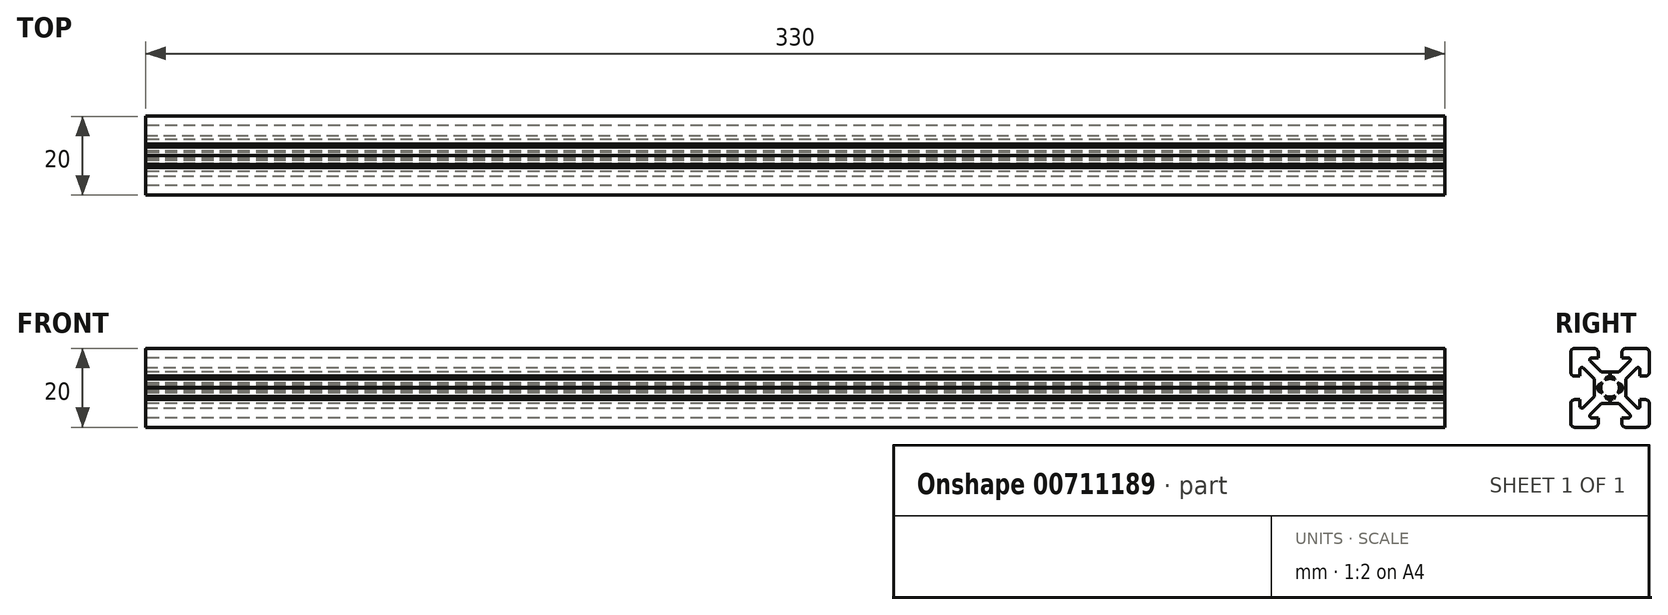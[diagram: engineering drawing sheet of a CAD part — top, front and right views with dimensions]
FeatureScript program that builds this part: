
annotation { "Feature Type Name" : "Feature", "Feature Type Description" : "" }
export const myFeature = defineFeature(function(context is Context, id is Id, definition is map)
    precondition{}
    {
        {
            var Q0;
            Q0=qCreatedBy(makeId("Top.planeOp"),FACE);
            var sketch = newSketch(context, id + "F0", { "sketchPlane" : qUnion([Q0])});
            skLineSegment(sketch, "E0", {"start": v(-15.81, 0) * mm, "end": v(2.4, 0) * mm, "construction": true});
            skLineSegment(sketch, "E1", {"start": v(0, 15.89) * mm, "end": v(0, -13.7) * mm, "construction": true});
            skLineSegment(sketch, "E2", {"start": v(0, 0) * mm, "end": v(-1.66, 1.66) * mm, "construction": true});
            skLineSegment(sketch, "E3", {"start": v(-2.3, 4.06) * mm, "end": v(-5.86, 7.63) * mm});
            skLineSegment(sketch, "E4", {"start": v(-5.86, 7.63) * mm, "end": v(-3, 7.63) * mm});
            skLineSegment(sketch, "E5", {"start": v(-3, 7.63) * mm, "end": v(-3, 10) * mm});
            skLineSegment(sketch, "E6", {"start": v(-3, 10) * mm, "end": v(-10, 10) * mm});
            skLineSegment(sketch, "E7.MirrorCS", {"start": v(-4, 2.23) * mm, "end": v(-7.63, 5.86) * mm});
            skLineSegment(sketch, "E8.MirrorCS", {"start": v(-7.63, 3) * mm, "end": v(-10, 3) * mm});
            skLineSegment(sketch, "E9.MirrorCS", {"start": v(-10, 3) * mm, "end": v(-10, 10) * mm});
            skLineSegment(sketch, "E10.MirrorCS", {"start": v(-7.63, 5.86) * mm, "end": v(-7.63, 3) * mm});
            skLineSegment(sketch, "E11.MirrorCS", {"start": v(3, 10) * mm, "end": v(10, 10) * mm});
            skLineSegment(sketch, "E12.MirrorCS", {"start": v(5.86, 7.63) * mm, "end": v(3, 7.63) * mm});
            skLineSegment(sketch, "E13.MirrorCS", {"start": v(3, 7.63) * mm, "end": v(3, 10) * mm});
            skLineSegment(sketch, "E14.MirrorCS", {"start": v(7.63, 5.86) * mm, "end": v(7.63, 3) * mm});
            skLineSegment(sketch, "E15.MirrorCS", {"start": v(10, 3) * mm, "end": v(10, 10) * mm});
            skLineSegment(sketch, "E16.MirrorCS", {"start": v(7.63, 3) * mm, "end": v(10, 3) * mm});
            skLineSegment(sketch, "E17.MirrorCS", {"start": v(2.3, 4.06) * mm, "end": v(5.86, 7.63) * mm});
            skLineSegment(sketch, "E18.MirrorCS", {"start": v(4, 2.23) * mm, "end": v(7.63, 5.86) * mm});
            skLineSegment(sketch, "E19.MirrorCS", {"start": v(5.86, -7.63) * mm, "end": v(3, -7.63) * mm});
            skLineSegment(sketch, "E20.MirrorCS", {"start": v(3, -10) * mm, "end": v(10, -10) * mm});
            skLineSegment(sketch, "E21.MirrorCS", {"start": v(-5.86, -7.63) * mm, "end": v(-3, -7.63) * mm});
            skLineSegment(sketch, "E22.MirrorCS", {"start": v(-3, -10) * mm, "end": v(-10, -10) * mm});
            skLineSegment(sketch, "E23.MirrorCS", {"start": v(-3, -7.63) * mm, "end": v(-3, -10) * mm});
            skLineSegment(sketch, "E24.MirrorCS", {"start": v(3, -7.63) * mm, "end": v(3, -10) * mm});
            skLineSegment(sketch, "E25.MirrorCS", {"start": v(7.63, -5.86) * mm, "end": v(7.63, -3) * mm});
            skLineSegment(sketch, "E26.MirrorCS", {"start": v(10, -3) * mm, "end": v(10, -10) * mm});
            skLineSegment(sketch, "E27.MirrorCS", {"start": v(4, -2.23) * mm, "end": v(7.63, -5.86) * mm});
            skLineSegment(sketch, "E28.MirrorCS", {"start": v(-7.63, -5.86) * mm, "end": v(-7.63, -3) * mm});
            skLineSegment(sketch, "E29.MirrorCS", {"start": v(-10, -3) * mm, "end": v(-10, -10) * mm});
            skLineSegment(sketch, "E30.MirrorCS", {"start": v(-7.63, -3) * mm, "end": v(-10, -3) * mm});
            skLineSegment(sketch, "E31.MirrorCS", {"start": v(-4, -2.23) * mm, "end": v(-7.63, -5.86) * mm});
            skLineSegment(sketch, "E32.MirrorCS", {"start": v(2.23, -4) * mm, "end": v(5.86, -7.63) * mm});
            skLineSegment(sketch, "E33.MirrorCS", {"start": v(-2.23, -4) * mm, "end": v(-5.86, -7.63) * mm});
            skLineSegment(sketch, "E34.MirrorCS", {"start": v(7.63, -3) * mm, "end": v(10, -3) * mm});
            skLineSegment(sketch, "E35", {"start": v(-4, 0) * mm, "end": v(-4, 0) * mm});
            skLineSegment(sketch, "E36", {"start": v(-2.3, 4.06) * mm, "end": v(-0.02, 4.06) * mm});
            skLineSegment(sketch, "E37.MirrorCS", {"start": v(-15.81, 8.12) * mm, "end": v(21.32, 8.12) * mm, "construction": true});
            skLineSegment(sketch, "E38", {"start": v(-4, 2.23) * mm, "end": v(-4, 0.02) * mm});
            skLineSegment(sketch, "E39", {"start": v(-2.23, -4) * mm, "end": v(-0.05, -4) * mm});
            skLineSegment(sketch, "E40", {"start": v(4, 2.23) * mm, "end": v(4, 0.03) * mm});
            skPoint(sketch, "E41.orphan", {"position": v(-0.59, 2.36) * mm});
            skPoint(sketch, "E42.orphan", {"position": v(-2.36, 0.59) * mm});
            skLineSegment(sketch, "E43.trimOffspring", {"start": v(0.03, 4.06) * mm, "end": v(2.3, 4.06) * mm});
            skPoint(sketch, "E44.orphan", {"position": v(0.59, 2.36) * mm});
            skPoint(sketch, "E45.orphan", {"position": v(2.36, 0.59) * mm});
            skPoint(sketch, "E46.orphan", {"position": v(-2.36, -0.59) * mm});
            skPoint(sketch, "E47.orphan", {"position": v(-0.59, -2.36) * mm});
            skPoint(sketch, "E48.orphan", {"position": v(0.59, -2.36) * mm});
            skPoint(sketch, "E49.orphan", {"position": v(2.36, -0.59) * mm});
            skLineSegment(sketch, "E50", {"start": v(-2.4, 0.03) * mm, "end": v(-2.4, 0.03) * mm});
            skLineSegment(sketch, "E51.MirrorCS", {"start": v(-2.4, -0.03) * mm, "end": v(-2.4, -0.03) * mm});
            skLineSegment(sketch, "E52.MirrorCS", {"start": v(2.4, 0.03) * mm, "end": v(2.4, 0.03) * mm});
            skLineSegment(sketch, "E53.MirrorCS", {"start": v(2.4, -0.03) * mm, "end": v(2.4, -0.03) * mm});
            skLineSegment(sketch, "E54.trimOffspring", {"start": v(4, -0.03) * mm, "end": v(4, -2.23) * mm});
            skLineSegment(sketch, "E55.trimOffspring", {"start": v(-4, -0.03) * mm, "end": v(-4, -2.23) * mm});
            skPoint(sketch, "E56.end.orphan", {"position": v(-2.4, 0) * mm});
            skPoint(sketch, "E57.orphan", {"position": v(-4, 0.03) * mm});
            skPoint(sketch, "E58.MirrorCS.end.orphan", {"position": v(2.4, 0) * mm});
            skPoint(sketch, "E58.MirrorCS.start.orphan", {"position": v(2.4, -0.03) * mm});
            skPoint(sketch, "E59.MirrorCS.start.orphan", {"position": v(2.4, 0.03) * mm});
            skLineSegment(sketch, "E60.trimOffspring", {"start": v(0.05, -4) * mm, "end": v(2.23, -4) * mm});
            skLineSegment(sketch, "E61", {"start": v(0, 0) * mm, "end": v(10, 10) * mm, "construction": true});
            skLineSegment(sketch, "E62", {"start": v(0, 0) * mm, "end": v(-10, -10) * mm, "construction": true});
            skLineSegment(sketch, "E63", {"start": v(10, -10) * mm, "end": v(0.07, 0.07) * mm, "construction": true});
            skPoint(sketch, "E64.start.orphan", {"position": v(-4, -0.03) * mm});
            skLineSegment(sketch, "E65", {"start": v(-2.82, -0.78) * mm, "end": v(-1.9, -1.37) * mm});
            skPoint(sketch, "E66.orphan", {"position": v(-1.66, -1.66) * mm});
            skPoint(sketch, "E67.orphan", {"position": v(0.03, -4.06) * mm});
            skPoint(sketch, "E68.orphan", {"position": v(-0.03, -4.06) * mm});
            skLineSegment(sketch, "E69", {"start": v(-2.82, 0.8) * mm, "end": v(-1.87, 1.41) * mm});
            skLineSegment(sketch, "E70", {"start": v(-0.76, 2.95) * mm, "end": v(-1.54, 1.77) * mm});
            skLineSegment(sketch, "E71", {"start": v(0.76, 2.95) * mm, "end": v(1.51, 1.8) * mm});
            skLineSegment(sketch, "E72", {"start": v(2.82, 0.8) * mm, "end": v(1.83, 1.46) * mm});
            skLineSegment(sketch, "E73", {"start": v(2.82, -0.8) * mm, "end": v(1.87, -1.41) * mm});
            skLineSegment(sketch, "E74.trimOffspring", {"start": v(1.8, -1.68) * mm, "end": v(1.82, -1.66) * mm});
            skLineSegment(sketch, "E75.trimOffspring", {"start": v(-8.12, 8.12) * mm, "end": v(-29.35, 29.35) * mm, "construction": true});
            skLineSegment(sketch, "E76", {"start": v(0.74, -2.96) * mm, "end": v(1.51, -1.8) * mm});
            skPoint(sketch, "E77.trimOffspring.start.orphan", {"position": v(0.33, -2.4) * mm});
            skPoint(sketch, "E78.MirrorCS.end.orphan", {"position": v(-0.33, -2.4) * mm});
            skLineSegment(sketch, "E79.trimOffspring", {"start": v(2.43, 0) * mm, "end": v(21.32, 0) * mm, "construction": true});
            skPoint(sketch, "E80.trimOffspring.start.orphan", {"position": v(0.33, 2.4) * mm});
            skPoint(sketch, "E81.trimOffspring.start.orphan", {"position": v(-0.33, 2.4) * mm});
            skArc(sketch, "E82", {"start": v(-1.87, 1.41) * mm, "mid": v(-2.35, 0.03) * mm, "end": v(-1.9, -1.37) * mm});
            skArc(sketch, "E83.trimOffspring", {"start": v(1.51, 1.8) * mm, "mid": v(-0.02, 2.35) * mm, "end": v(-1.54, 1.77) * mm});
            skArc(sketch, "E84.trimOffspring", {"start": v(1.87, -1.41) * mm, "mid": v(2.35, 0.03) * mm, "end": v(1.83, 1.46) * mm});
            skArc(sketch, "E85.trimOffspring", {"start": v(-1.55, -1.76) * mm, "mid": v(-0.03, -2.35) * mm, "end": v(1.51, -1.8) * mm});
            skLineSegment(sketch, "E86", {"start": v(-1.55, -1.76) * mm, "end": v(-0.75, -2.96) * mm});
            skLineSegment(sketch, "E87", {"start": v(-4, 0.03) * mm, "end": v(-2.82, 0.03) * mm});
            skLineSegment(sketch, "E88", {"start": v(-2.82, 0.03) * mm, "end": v(-2.82, 0.8) * mm});
            skLineSegment(sketch, "E89", {"start": v(-4, -0.03) * mm, "end": v(-2.82, -0.03) * mm});
            skLineSegment(sketch, "E90", {"start": v(-2.82, -0.03) * mm, "end": v(-2.82, -0.78) * mm});
            skLineSegment(sketch, "E91.MirrorCS", {"start": v(4, 0.03) * mm, "end": v(2.82, 0.03) * mm});
            skLineSegment(sketch, "E92.MirrorCS", {"start": v(4, -0.03) * mm, "end": v(2.82, -0.03) * mm});
            skLineSegment(sketch, "E93", {"start": v(2.82, 0.03) * mm, "end": v(2.82, 0.8) * mm});
            skLineSegment(sketch, "E94", {"start": v(2.82, -0.03) * mm, "end": v(2.82, -0.8) * mm});
            skLineSegment(sketch, "E95", {"start": v(-0.05, -4) * mm, "end": v(-0.05, -2.96) * mm});
            skLineSegment(sketch, "E96", {"start": v(-0.05, -2.96) * mm, "end": v(-0.75, -2.96) * mm});
            skLineSegment(sketch, "E97", {"start": v(0.05, -4) * mm, "end": v(0.05, -2.96) * mm});
            skLineSegment(sketch, "E98", {"start": v(0.05, -2.96) * mm, "end": v(0.74, -2.96) * mm});
            skLineSegment(sketch, "E99", {"start": v(-0.02, 4.06) * mm, "end": v(-0.02, 2.95) * mm});
            skLineSegment(sketch, "E100", {"start": v(-0.02, 2.95) * mm, "end": v(-0.76, 2.95) * mm});
            skLineSegment(sketch, "E101", {"start": v(0.03, 4.06) * mm, "end": v(0.03, 2.95) * mm});
            skLineSegment(sketch, "E102", {"start": v(0.03, 2.95) * mm, "end": v(0.76, 2.95) * mm});
            skSolve(sketch);
        }
        {
            var Q0;
            Q0=qSketchRegion(id+"F0",true);
            extrude(context, id + "F1", {"entities" : qUnion([Q0]), "depth" : 330 * mm});
        }
        {
            var Q0;
            Q0=makeQuery(id+"F1.opExtrude","SWEPT_EDGE",EDGE,{"disambiguationData":[OSD([sQuery(id+"F0.wireOp",EDGE,"E15.MirrorCS"),sQuery(id+"F0.wireOp",EDGE,"E11.MirrorCS")])]});
            var Q1;
            Q1=makeQuery(id+"F1.opExtrude","SWEPT_EDGE",EDGE,{"disambiguationData":[OSD([sQuery(id+"F0.wireOp",EDGE,"E20.MirrorCS"),sQuery(id+"F0.wireOp",EDGE,"E26.MirrorCS")])]});
            var Q2;
            Q2=makeQuery(id+"F1.opExtrude","SWEPT_EDGE",EDGE,{"disambiguationData":[OSD([sQuery(id+"F0.wireOp",EDGE,"E22.MirrorCS"),sQuery(id+"F0.wireOp",EDGE,"E29.MirrorCS")])]});
            var Q3;
            Q3=makeQuery(id+"F1.opExtrude","SWEPT_EDGE",EDGE,{"disambiguationData":[OSD([sQuery(id+"F0.wireOp",EDGE,"E22.MirrorCS"),sQuery(id+"F0.wireOp",EDGE,"E23.MirrorCS")])]});
            var Q4;
            Q4=makeQuery(id+"F1.opExtrude","SWEPT_EDGE",EDGE,{"disambiguationData":[OSD([sQuery(id+"F0.wireOp",EDGE,"E20.MirrorCS"),sQuery(id+"F0.wireOp",EDGE,"E24.MirrorCS")])]});
            var Q5;
            Q5=makeQuery(id+"F1.opExtrude","SWEPT_EDGE",EDGE,{"disambiguationData":[OSD([sQuery(id+"F0.wireOp",EDGE,"E5"),sQuery(id+"F0.wireOp",EDGE,"E6")])]});
            var Q6;
            Q6=makeQuery(id+"F1.opExtrude","SWEPT_EDGE",EDGE,{"disambiguationData":[OSD([sQuery(id+"F0.wireOp",EDGE,"E8.MirrorCS"),sQuery(id+"F0.wireOp",EDGE,"E9.MirrorCS")])]});
            var Q7;
            Q7=makeQuery(id+"F1.opExtrude","SWEPT_EDGE",EDGE,{"disambiguationData":[OSD([sQuery(id+"F0.wireOp",EDGE,"E15.MirrorCS"),sQuery(id+"F0.wireOp",EDGE,"E16.MirrorCS")])]});
            var Q8;
            Q8=makeQuery(id+"F1.opExtrude","SWEPT_EDGE",EDGE,{"disambiguationData":[OSD([sQuery(id+"F0.wireOp",EDGE,"E26.MirrorCS"),sQuery(id+"F0.wireOp",EDGE,"E34.MirrorCS")])]});
            var Q9;
            Q9=makeQuery(id+"F1.opExtrude","SWEPT_EDGE",EDGE,{"disambiguationData":[OSD([sQuery(id+"F0.wireOp",EDGE,"E29.MirrorCS"),sQuery(id+"F0.wireOp",EDGE,"E30.MirrorCS")])]});
            var Q10;
            Q10=makeQuery(id+"F1.opExtrude","SWEPT_EDGE",EDGE,{"disambiguationData":[OSD([sQuery(id+"F0.wireOp",EDGE,"E9.MirrorCS"),sQuery(id+"F0.wireOp",EDGE,"E6")])]});
            var Q11;
            Q11=makeQuery(id+"F1.opExtrude","SWEPT_EDGE",EDGE,{"disambiguationData":[OSD([sQuery(id+"F0.wireOp",EDGE,"E13.MirrorCS"),sQuery(id+"F0.wireOp",EDGE,"E11.MirrorCS")])]});
            fillet(context, id + "F2", {"entities" : qUnion([Q0, Q1, Q2, Q3, Q4, Q5, Q6, Q7, Q8, Q9, Q10, Q11]), "radius" : 1 * mm, "tangentPropagation" : true, "allowEdgeOverflow" : false});
        }
        {
            var Q0;
            Q0=makeQuery(id+"F1.opExtrude","SWEPT_EDGE",EDGE,{"disambiguationData":[OSD([sQuery(id+"F0.wireOp",EDGE,"E7.MirrorCS"),sQuery(id+"F0.wireOp",EDGE,"E10.MirrorCS")])]});
            var Q1;
            Q1=makeQuery(id+"F1.opExtrude","SWEPT_EDGE",EDGE,{"disambiguationData":[OSD([sQuery(id+"F0.wireOp",EDGE,"E3"),sQuery(id+"F0.wireOp",EDGE,"E4")])]});
            var Q2;
            Q2=makeQuery(id+"F1.opExtrude","SWEPT_EDGE",EDGE,{"disambiguationData":[OSD([sQuery(id+"F0.wireOp",EDGE,"E12.MirrorCS"),sQuery(id+"F0.wireOp",EDGE,"E17.MirrorCS")])]});
            var Q3;
            Q3=makeQuery(id+"F1.opExtrude","SWEPT_EDGE",EDGE,{"disambiguationData":[OSD([sQuery(id+"F0.wireOp",EDGE,"E14.MirrorCS"),sQuery(id+"F0.wireOp",EDGE,"E18.MirrorCS")])]});
            var Q4;
            Q4=makeQuery(id+"F1.opExtrude","SWEPT_EDGE",EDGE,{"disambiguationData":[OSD([sQuery(id+"F0.wireOp",EDGE,"E28.MirrorCS"),sQuery(id+"F0.wireOp",EDGE,"E31.MirrorCS")])]});
            var Q5;
            Q5=makeQuery(id+"F1.opExtrude","SWEPT_EDGE",EDGE,{"disambiguationData":[OSD([sQuery(id+"F0.wireOp",EDGE,"E21.MirrorCS"),sQuery(id+"F0.wireOp",EDGE,"E33.MirrorCS")])]});
            var Q6;
            Q6=makeQuery(id+"F1.opExtrude","SWEPT_EDGE",EDGE,{"disambiguationData":[OSD([sQuery(id+"F0.wireOp",EDGE,"E19.MirrorCS"),sQuery(id+"F0.wireOp",EDGE,"E32.MirrorCS")])]});
            var Q7;
            Q7=makeQuery(id+"F1.opExtrude","SWEPT_EDGE",EDGE,{"disambiguationData":[OSD([sQuery(id+"F0.wireOp",EDGE,"E25.MirrorCS"),sQuery(id+"F0.wireOp",EDGE,"E27.MirrorCS")])]});
            fillet(context, id + "F3", {"entities" : qUnion([Q0, Q1, Q2, Q3, Q4, Q5, Q6, Q7]), "radius" : .5 * mm, "tangentPropagation" : true, "allowEdgeOverflow" : false});
        }
        {
            var Q0;
            Q0=makeQuery(id+"F1.opExtrude","SWEPT_EDGE",EDGE,{"disambiguationData":[OSD([sQuery(id+"F0.wireOp",EDGE,"E69"),sQuery(id+"F0.wireOp",EDGE,"E82")])]});
            var Q1;
            Q1=makeQuery(id+"F1.opExtrude","SWEPT_EDGE",EDGE,{"disambiguationData":[OSD([sQuery(id+"F0.wireOp",EDGE,"E17.MirrorCS"),sQuery(id+"F0.wireOp",EDGE,"E43.trimOffspring")])]});
            var Q2;
            {var subQ0=sQuery(id+"F0.wireOp",EDGE,"E12.MirrorCS");Q2=makeQuery(id+"F3.opFillet","BLEND_EDGE",EDGE,{"blendedFrom":[makeQuery(id+"F1.opExtrude","SWEPT_EDGE",EDGE,{"disambiguationData":[OSD([subQ0,sQuery(id+"F0.wireOp",EDGE,"E17.MirrorCS")])]}),makeQuery(id+"F1.opExtrude","SWEPT_FACE",FACE,{"disambiguationData":[OSD([subQ0])]})],"blendedInto":[makeQuery(id+"F1.opExtrude","SWEPT_FACE",FACE,{"disambiguationData":[OSD([subQ0])]})]});}
            var Q3;
            Q3=makeQuery(id+"F1.opExtrude","SWEPT_EDGE",EDGE,{"disambiguationData":[OSD([sQuery(id+"F0.wireOp",EDGE,"E70"),sQuery(id+"F0.wireOp",EDGE,"E83.trimOffspring")])]});
            var Q4;
            Q4=makeQuery(id+"F1.opExtrude","SWEPT_EDGE",EDGE,{"disambiguationData":[OSD([sQuery(id+"F0.wireOp",EDGE,"VnvyymTW-JKNP-Vp1J-SOXt-zXPDHYCny5Fm"),sQuery(id+"F0.wireOp",EDGE,"E85.trimOffspring")])]});
            var Q5;
            Q5=makeQuery(id+"F1.opExtrude","SWEPT_EDGE",EDGE,{"disambiguationData":[OSD([sQuery(id+"F0.wireOp",EDGE,"E76"),sQuery(id+"F0.wireOp",EDGE,"E85.trimOffspring")])]});
            var Q6;
            Q6=makeQuery(id+"F1.opExtrude","SWEPT_EDGE",EDGE,{"disambiguationData":[OSD([sQuery(id+"F0.wireOp",EDGE,"E73"),sQuery(id+"F0.wireOp",EDGE,"E84.trimOffspring")])]});
            var Q7;
            Q7=makeQuery(id+"F1.opExtrude","SWEPT_EDGE",EDGE,{"disambiguationData":[OSD([sQuery(id+"F0.wireOp",EDGE,"E72"),sQuery(id+"F0.wireOp",EDGE,"E84.trimOffspring")])]});
            var Q8;
            Q8=makeQuery(id+"F1.opExtrude","SWEPT_EDGE",EDGE,{"disambiguationData":[OSD([sQuery(id+"F0.wireOp",EDGE,"E71"),sQuery(id+"F0.wireOp",EDGE,"E83.trimOffspring")])]});
            var Q9;
            Q9=makeQuery(id+"F1.opExtrude","SWEPT_EDGE",EDGE,{"disambiguationData":[OSD([sQuery(id+"F0.wireOp",EDGE,"E65"),sQuery(id+"F0.wireOp",EDGE,"E82")])]});
            fillet(context, id + "F4", {"entities" : qUnion([Q0, Q1, Q2, Q3, Q4, Q5, Q6, Q7, Q8, Q9]), "radius" : .1 * mm, "tangentPropagation" : true, "allowEdgeOverflow" : false});
        }
        {
            var Q0;
            Q0=makeQuery(id+"F1.opExtrude","SWEPT_BODY",BODY,{"disambiguationData":[OSD([sQuery(id+"F0.wireOp",EDGE,"E3"),sQuery(id+"F0.wireOp",EDGE,"E7.MirrorCS"),sQuery(id+"F0.wireOp",EDGE,"E8.MirrorCS"),sQuery(id+"F0.wireOp",EDGE,"E9.MirrorCS"),sQuery(id+"F0.wireOp",EDGE,"E10.MirrorCS"),sQuery(id+"F0.wireOp",EDGE,"E5"),sQuery(id+"F0.wireOp",EDGE,"E6"),sQuery(id+"F0.wireOp",EDGE,"E4"),sQuery(id+"F0.wireOp",EDGE,"E14.MirrorCS"),sQuery(id+"F0.wireOp",EDGE,"E15.MirrorCS"),sQuery(id+"F0.wireOp",EDGE,"E16.MirrorCS"),sQuery(id+"F0.wireOp",EDGE,"E12.MirrorCS"),sQuery(id+"F0.wireOp",EDGE,"E17.MirrorCS"),sQuery(id+"F0.wireOp",EDGE,"E18.MirrorCS"),sQuery(id+"F0.wireOp",EDGE,"E13.MirrorCS"),sQuery(id+"F0.wireOp",EDGE,"E11.MirrorCS"),sQuery(id+"F0.wireOp",EDGE,"E21.MirrorCS"),sQuery(id+"F0.wireOp",EDGE,"E19.MirrorCS"),sQuery(id+"F0.wireOp",EDGE,"E20.MirrorCS"),sQuery(id+"F0.wireOp",EDGE,"E24.MirrorCS"),sQuery(id+"F0.wireOp",EDGE,"E25.MirrorCS"),sQuery(id+"F0.wireOp",EDGE,"E26.MirrorCS"),sQuery(id+"F0.wireOp",EDGE,"E27.MirrorCS"),sQuery(id+"F0.wireOp",EDGE,"E22.MirrorCS"),sQuery(id+"F0.wireOp",EDGE,"E28.MirrorCS"),sQuery(id+"F0.wireOp",EDGE,"E29.MirrorCS"),sQuery(id+"F0.wireOp",EDGE,"E30.MirrorCS"),sQuery(id+"F0.wireOp",EDGE,"E31.MirrorCS"),sQuery(id+"F0.wireOp",EDGE,"E23.MirrorCS"),sQuery(id+"F0.wireOp",EDGE,"E32.MirrorCS"),sQuery(id+"F0.wireOp",EDGE,"E33.MirrorCS"),sQuery(id+"F0.wireOp",EDGE,"E34.MirrorCS"),sQuery(id+"F0.wireOp",EDGE,"E36"),sQuery(id+"F0.wireOp",EDGE,"E38"),sQuery(id+"F0.wireOp",EDGE,"E39"),sQuery(id+"F0.wireOp",EDGE,"E40"),sQuery(id+"F0.wireOp",EDGE,"E43.trimOffspring"),sQuery(id+"F0.wireOp",EDGE,"E54.trimOffspring"),sQuery(id+"F0.wireOp",EDGE,"E55.trimOffspring"),sQuery(id+"F0.wireOp",EDGE,"E60.trimOffspring"),sQuery(id+"F0.wireOp",EDGE,"E65"),sQuery(id+"F0.wireOp",EDGE,"E69"),sQuery(id+"F0.wireOp",EDGE,"E70"),sQuery(id+"F0.wireOp",EDGE,"E71"),sQuery(id+"F0.wireOp",EDGE,"E72"),sQuery(id+"F0.wireOp",EDGE,"E73"),sQuery(id+"F0.wireOp",EDGE,"E76"),sQuery(id+"F0.wireOp",EDGE,"E82"),sQuery(id+"F0.wireOp",EDGE,"E83.trimOffspring"),sQuery(id+"F0.wireOp",EDGE,"E84.trimOffspring"),sQuery(id+"F0.wireOp",EDGE,"E85.trimOffspring"),sQuery(id+"F0.wireOp",EDGE,"E86"),sQuery(id+"F0.wireOp",EDGE,"E87"),sQuery(id+"F0.wireOp",EDGE,"E88"),sQuery(id+"F0.wireOp",EDGE,"E89"),sQuery(id+"F0.wireOp",EDGE,"E90"),sQuery(id+"F0.wireOp",EDGE,"E91.MirrorCS"),sQuery(id+"F0.wireOp",EDGE,"E92.MirrorCS"),sQuery(id+"F0.wireOp",EDGE,"E93"),sQuery(id+"F0.wireOp",EDGE,"E94"),sQuery(id+"F0.wireOp",EDGE,"E95"),sQuery(id+"F0.wireOp",EDGE,"E96"),sQuery(id+"F0.wireOp",EDGE,"E97"),sQuery(id+"F0.wireOp",EDGE,"E98"),sQuery(id+"F0.wireOp",EDGE,"E99"),sQuery(id+"F0.wireOp",EDGE,"E100"),sQuery(id+"F0.wireOp",EDGE,"E101"),sQuery(id+"F0.wireOp",EDGE,"E102")])]});
            var Q1;
            Q1=makeQuery(id+"F1.opExtrude","CAP_EDGE",EDGE,{"disambiguationData":[OSD([sQuery(id+"F0.wireOp",EDGE,"E15.MirrorCS")])],"isStart":false});
            transform(context, id + "F5", {"entities" : qUnion([Q0]), "transformType" : TransformType.ROTATION, "transformAxis" : qUnion([Q1]), "angle" : 90 * degree, "makeCopy" : false});
        }
        {
            var Q0;
            Q0=makeQuery(id+"F1.opExtrude","SWEPT_BODY",BODY,{"disambiguationData":[OSD([sQuery(id+"F0.wireOp",EDGE,"E3"),sQuery(id+"F0.wireOp",EDGE,"E7.MirrorCS"),sQuery(id+"F0.wireOp",EDGE,"E8.MirrorCS"),sQuery(id+"F0.wireOp",EDGE,"E9.MirrorCS"),sQuery(id+"F0.wireOp",EDGE,"E10.MirrorCS"),sQuery(id+"F0.wireOp",EDGE,"E5"),sQuery(id+"F0.wireOp",EDGE,"E6"),sQuery(id+"F0.wireOp",EDGE,"E4"),sQuery(id+"F0.wireOp",EDGE,"E14.MirrorCS"),sQuery(id+"F0.wireOp",EDGE,"E15.MirrorCS"),sQuery(id+"F0.wireOp",EDGE,"E16.MirrorCS"),sQuery(id+"F0.wireOp",EDGE,"E12.MirrorCS"),sQuery(id+"F0.wireOp",EDGE,"E17.MirrorCS"),sQuery(id+"F0.wireOp",EDGE,"E18.MirrorCS"),sQuery(id+"F0.wireOp",EDGE,"E13.MirrorCS"),sQuery(id+"F0.wireOp",EDGE,"E11.MirrorCS"),sQuery(id+"F0.wireOp",EDGE,"E21.MirrorCS"),sQuery(id+"F0.wireOp",EDGE,"E19.MirrorCS"),sQuery(id+"F0.wireOp",EDGE,"E20.MirrorCS"),sQuery(id+"F0.wireOp",EDGE,"E24.MirrorCS"),sQuery(id+"F0.wireOp",EDGE,"E25.MirrorCS"),sQuery(id+"F0.wireOp",EDGE,"E26.MirrorCS"),sQuery(id+"F0.wireOp",EDGE,"E27.MirrorCS"),sQuery(id+"F0.wireOp",EDGE,"E22.MirrorCS"),sQuery(id+"F0.wireOp",EDGE,"E28.MirrorCS"),sQuery(id+"F0.wireOp",EDGE,"E29.MirrorCS"),sQuery(id+"F0.wireOp",EDGE,"E30.MirrorCS"),sQuery(id+"F0.wireOp",EDGE,"E31.MirrorCS"),sQuery(id+"F0.wireOp",EDGE,"E23.MirrorCS"),sQuery(id+"F0.wireOp",EDGE,"E32.MirrorCS"),sQuery(id+"F0.wireOp",EDGE,"E33.MirrorCS"),sQuery(id+"F0.wireOp",EDGE,"E34.MirrorCS"),sQuery(id+"F0.wireOp",EDGE,"E36"),sQuery(id+"F0.wireOp",EDGE,"E38"),sQuery(id+"F0.wireOp",EDGE,"E39"),sQuery(id+"F0.wireOp",EDGE,"E40"),sQuery(id+"F0.wireOp",EDGE,"E43.trimOffspring"),sQuery(id+"F0.wireOp",EDGE,"E54.trimOffspring"),sQuery(id+"F0.wireOp",EDGE,"E55.trimOffspring"),sQuery(id+"F0.wireOp",EDGE,"E60.trimOffspring"),sQuery(id+"F0.wireOp",EDGE,"E65"),sQuery(id+"F0.wireOp",EDGE,"E69"),sQuery(id+"F0.wireOp",EDGE,"E70"),sQuery(id+"F0.wireOp",EDGE,"E71"),sQuery(id+"F0.wireOp",EDGE,"E72"),sQuery(id+"F0.wireOp",EDGE,"E73"),sQuery(id+"F0.wireOp",EDGE,"E76"),sQuery(id+"F0.wireOp",EDGE,"E82"),sQuery(id+"F0.wireOp",EDGE,"E83.trimOffspring"),sQuery(id+"F0.wireOp",EDGE,"E84.trimOffspring"),sQuery(id+"F0.wireOp",EDGE,"E85.trimOffspring"),sQuery(id+"F0.wireOp",EDGE,"E86"),sQuery(id+"F0.wireOp",EDGE,"E87"),sQuery(id+"F0.wireOp",EDGE,"E88"),sQuery(id+"F0.wireOp",EDGE,"E89"),sQuery(id+"F0.wireOp",EDGE,"E90"),sQuery(id+"F0.wireOp",EDGE,"E91.MirrorCS"),sQuery(id+"F0.wireOp",EDGE,"E92.MirrorCS"),sQuery(id+"F0.wireOp",EDGE,"E93"),sQuery(id+"F0.wireOp",EDGE,"E94"),sQuery(id+"F0.wireOp",EDGE,"E95"),sQuery(id+"F0.wireOp",EDGE,"E96"),sQuery(id+"F0.wireOp",EDGE,"E97"),sQuery(id+"F0.wireOp",EDGE,"E98"),sQuery(id+"F0.wireOp",EDGE,"E99"),sQuery(id+"F0.wireOp",EDGE,"E100"),sQuery(id+"F0.wireOp",EDGE,"E101"),sQuery(id+"F0.wireOp",EDGE,"E102")])]});
            transform(context, id + "F6", {"entities" : qUnion([Q0]), "transformType" : TransformType.TRANSLATION_3D, "dx" : 421.9 * mm, "dy" : -525.53 * mm, "dz" : 0 * mm, "makeCopy" : false});
        }
    });
